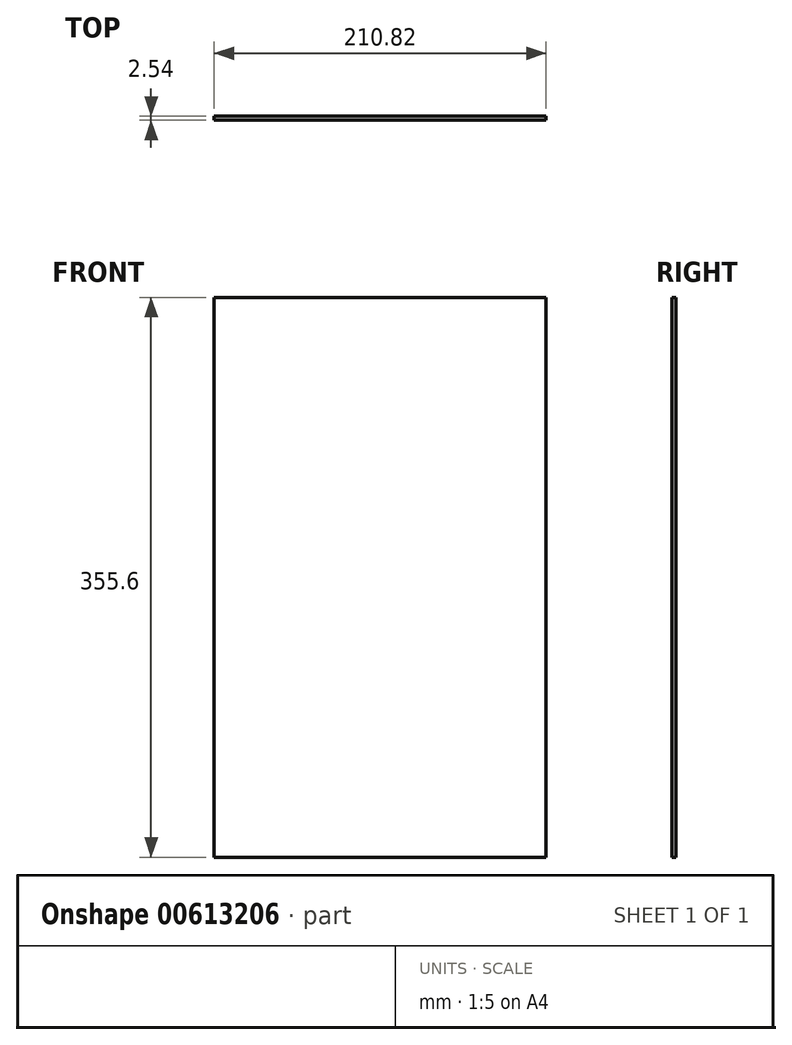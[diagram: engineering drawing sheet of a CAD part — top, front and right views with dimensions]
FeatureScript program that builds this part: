
annotation { "Feature Type Name" : "Feature", "Feature Type Description" : "" }
export const myFeature = defineFeature(function(context is Context, id is Id, definition is map)
    precondition{}
    {
        {
            var Q0;
            Q0=qCreatedBy(makeId("Front.planeOp"),FACE);
            var sketch = newSketch(context, id + "F0", { "sketchPlane" : qUnion([Q0])});
            skLineSegment(sketch, "E0", {"start": v(-132.8, -48.78) * mm, "end": v(-132.8, 306.82) * mm});
            skLineSegment(sketch, "E1", {"start": v(-132.8, -48.78) * mm, "end": v(78.02, -48.78) * mm});
            skLineSegment(sketch, "E2", {"start": v(78.02, -48.78) * mm, "end": v(78.02, 306.82) * mm});
            skLineSegment(sketch, "E3", {"start": v(78.02, 306.82) * mm, "end": v(-132.8, 306.82) * mm});
            skSolve(sketch);
        }
        {
            var Q0;
            Q0 = qSketchRegion(id + "F0", true);
            var Q1;
            Q1=makeQuery(id+"F0.imprint","IMPRINT",FACE,{"disambiguationData":[TD([[makeQuery(id+"F0.imprint","IMPRINT",EDGE,{"derivedFrom":sQuery(id+"F0.wireOp",EDGE,"E0")}),-1.0]])]});
            extrude(context, id + "F1", {"entities" : qUnion([Q0, Q1]), "depth" : 2.54 * mm, "offsetDistance" : 25.4 * mm});
        }
    });
